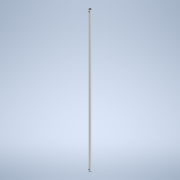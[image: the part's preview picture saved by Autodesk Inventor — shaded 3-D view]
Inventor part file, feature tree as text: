
AUTODESK INVENTOR PART (.ipt)
format: ipt  version: 2022 (Build 260153000, 153)  size: 169,984 bytes
history: native  units: mm
features: extrude x2, sketch x2
ambient origin geometry x8: Origin, YZ Plane, XZ Plane, XY Plane, X Axis, Y Axis, Z Axis, Center Point
bodies: Body1 (feature_tree)
feature tree (4):
  extrude  "Extrusion5"  Depth=7.0mm
  extrude  "Extrusion6"  Depth=10.0mm TaperAngle=0.0deg
  sketch  "Sketch2"  dims[d31=34.456mm d91=7.0mm]
  sketch  "Sketch3"  dims[d92=5.0mm d93=500.0mm d94=0.0mm d95=6.0mm d96=3.0mm d97=6.0mm d98=3.0mm d99=10.0mm d100=10.0mm d101=0.0mm d102=0.0mm]
